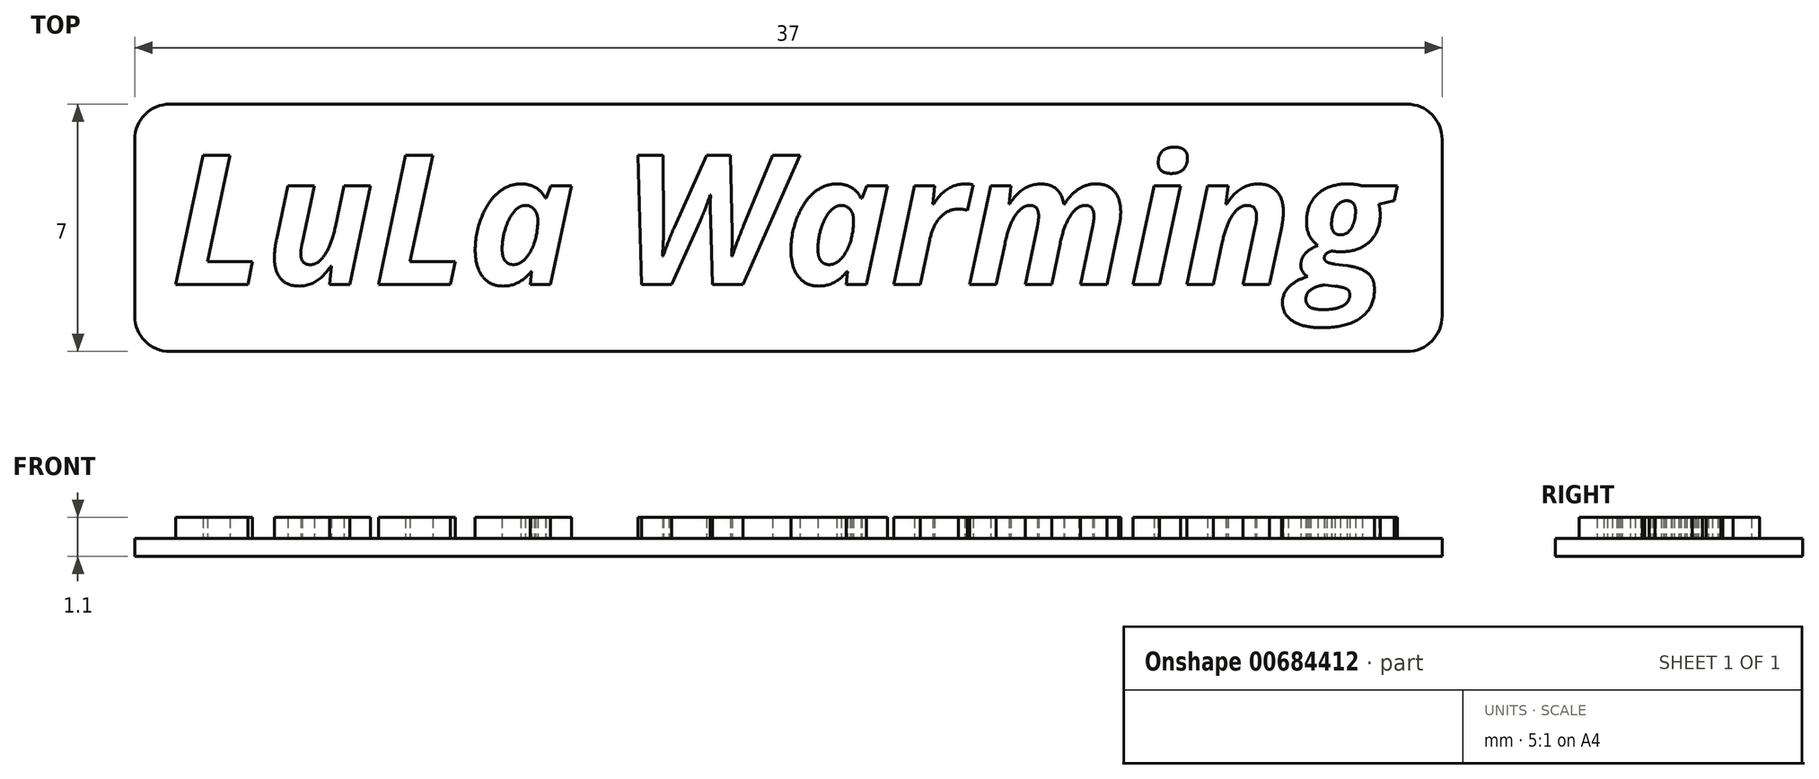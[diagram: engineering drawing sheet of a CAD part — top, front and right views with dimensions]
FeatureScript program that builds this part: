
annotation { "Feature Type Name" : "Feature", "Feature Type Description" : "" }
export const myFeature = defineFeature(function(context is Context, id is Id, definition is map)
    precondition{}
    {
        {
            var Q0;
            Q0=qCreatedBy(makeId("Top.planeOp"),FACE);
            var sketch = newSketch(context, id + "F0", { "sketchPlane" : qUnion([Q0])});
            skLineSegment(sketch, "E0.bottom", {"start": v(-17.5, 3.5) * mm, "end": v(17.5, 3.5) * mm});
            skLineSegment(sketch, "E0.top", {"start": v(-17.5, -3.5) * mm, "end": v(17.5, -3.5) * mm});
            skLineSegment(sketch, "E0.left", {"start": v(-18.5, 2.5) * mm, "end": v(-18.5, -2.5) * mm});
            skLineSegment(sketch, "E0.right", {"start": v(18.5, 2.5) * mm, "end": v(18.5, -2.5) * mm});
            skPoint(sketch, "E0.middle", {"position": v(0, 0) * mm});
            skPoint(sketch, "E1.visualSharp", {"position": v(-18.5, 3.5) * mm});
            skArc(sketch, "E1.filletArc", {"start": v(-17.5, 3.5) * mm, "mid": v(-18.2, 3.2) * mm, "end": v(-18.5, 2.5) * mm});
            skPoint(sketch, "E2.visualSharp", {"position": v(-18.5, -3.5) * mm});
            skArc(sketch, "E2.filletArc", {"start": v(-18.5, -2.5) * mm, "mid": v(-18.2, -3.2) * mm, "end": v(-17.5, -3.5) * mm});
            skPoint(sketch, "E3.visualSharp", {"position": v(18.5, -3.5) * mm});
            skArc(sketch, "E3.filletArc", {"start": v(17.5, -3.5) * mm, "mid": v(18.2, -3.2) * mm, "end": v(18.5, -2.5) * mm});
            skPoint(sketch, "E4.visualSharp", {"position": v(18.5, 3.5) * mm});
            skArc(sketch, "E4.filletArc", {"start": v(18.5, 2.5) * mm, "mid": v(18.2, 3.2) * mm, "end": v(17.5, 3.5) * mm});
            skSolve(sketch);
        }
        {
            var Q0;
            Q0=makeQuery(id+"F0.imprint","IMPRINT",FACE,{"disambiguationData":[TD([[makeQuery(id+"F0.imprint","IMPRINT",EDGE,{"derivedFrom":sQuery(id+"F0.wireOp",EDGE,"E0.bottom")}),-1.0]])]});
            extrude(context, id + "F1", {"entities" : qUnion([Q0]), "depth" : .5 * mm, "offsetDistance" : 25 * mm});
        }
        {
            var Q0;
            Q0=makeQuery(id+"F1.opExtrude","CAP_FACE",FACE,{"disambiguationData":[OSD([sQuery(id+"F0.wireOp",EDGE,"E0.bottom"),sQuery(id+"F0.wireOp",EDGE,"E0.top"),sQuery(id+"F0.wireOp",EDGE,"E0.left"),sQuery(id+"F0.wireOp",EDGE,"E0.right")])],"isStart":false});
            var sketch = newSketch(context, id + "F2", { "sketchPlane" : qUnion([Q0])});
            skText(sketch, "E5", { "text": "LuLa Warming", "fontName": "OpenSans-BoldItalic.ttf"});
            const initialGuessF2  = {"E5": [-0.01747, -0.0016, 1, 0, 0.00368]};
            skSetInitialGuess(sketch, initialGuessF2);
            skSolve(sketch);
        }
        {
            var Q0;
            Q0 = qSketchRegion(id + "F2", true);
            extrude(context, id + "F3", {"entities" : qUnion([Q0]), "operationType" : NewBodyOperationType.ADD, "depth" : .6 * mm, "offsetDistance" : 25 * mm});
        }
    });
